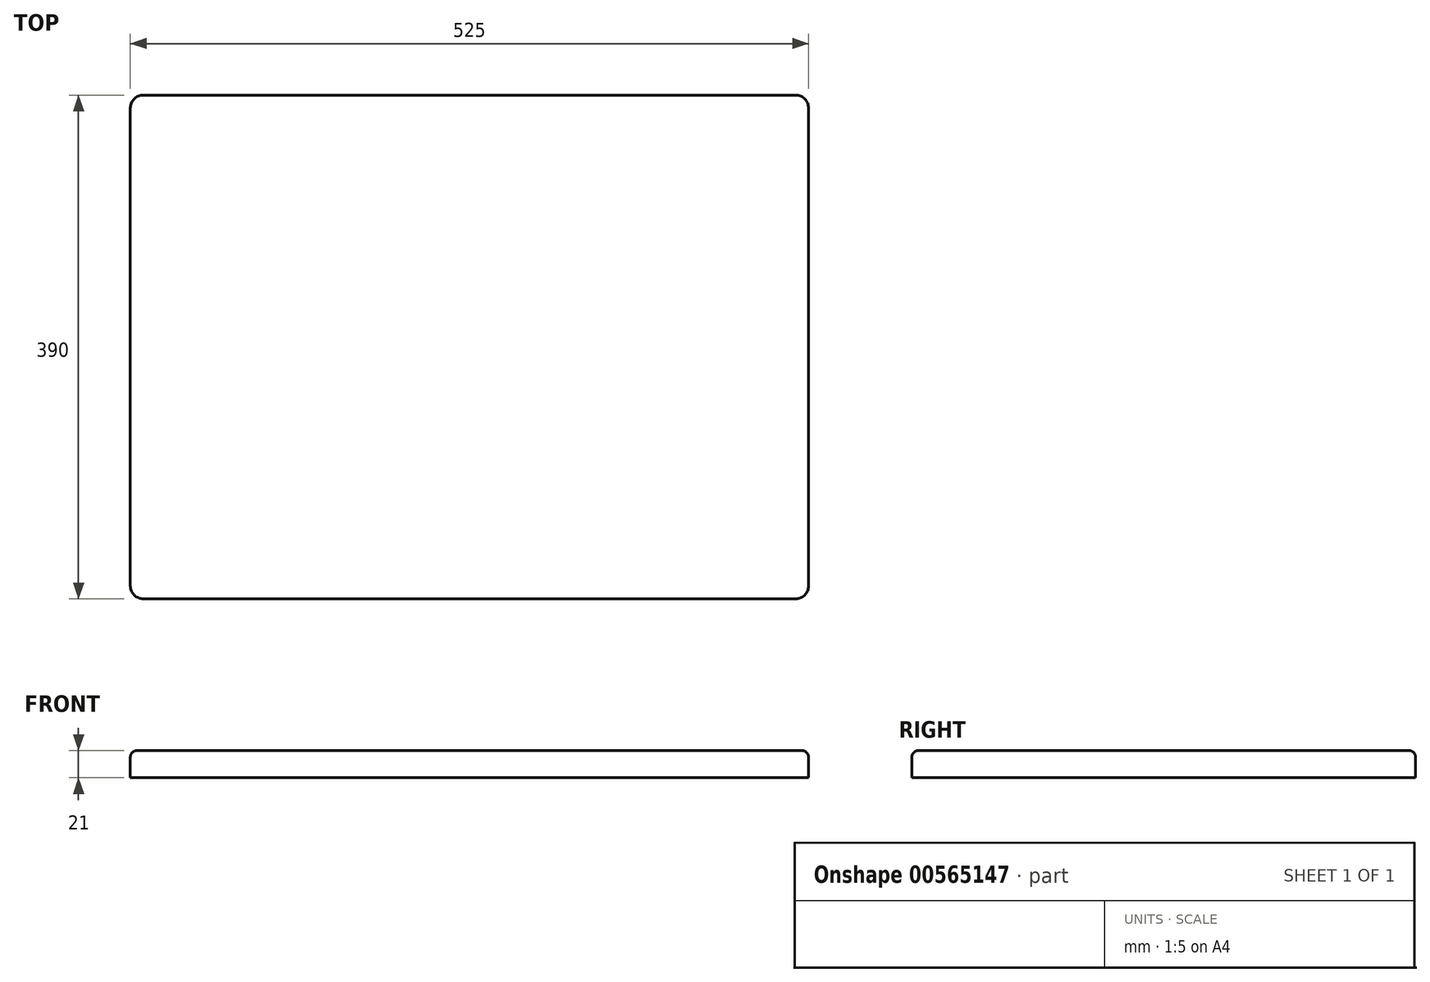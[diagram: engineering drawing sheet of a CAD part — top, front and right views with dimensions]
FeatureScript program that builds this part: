
annotation { "Feature Type Name" : "Feature", "Feature Type Description" : "" }
export const myFeature = defineFeature(function(context is Context, id is Id, definition is map)
    precondition{}
    {
        {
            var Q0;
            Q0=qCreatedBy(makeId("Top.planeOp"),FACE);
            var sketch = newSketch(context, id + "F0", { "sketchPlane" : qUnion([Q0])});
            skLineSegment(sketch, "E0.bottom", {"start": v(262.5, 195) * mm, "end": v(-262.5, 195) * mm});
            skLineSegment(sketch, "E0.top", {"start": v(262.5, -195) * mm, "end": v(-262.5, -195) * mm});
            skLineSegment(sketch, "E0.left", {"start": v(262.5, 195) * mm, "end": v(262.5, -195) * mm});
            skLineSegment(sketch, "E0.right", {"start": v(-262.5, 195) * mm, "end": v(-262.5, -195) * mm});
            skPoint(sketch, "E0.middle", {"position": v(0, 0) * mm});
            skSolve(sketch);
        }
        {
            var Q0;
            Q0=makeQuery(id+"F0.imprint","IMPRINT",FACE,{"disambiguationData":[TD([[makeQuery(id+"F0.imprint","IMPRINT",EDGE,{"derivedFrom":sQuery(id+"F0.wireOp",EDGE,"E0.bottom")}),1.0]])]});
            extrude(context, id + "F1", {"entities" : qUnion([Q0]), "depth" : 21 * mm, "offsetDistance" : 25 * mm});
        }
        {
            var Q0;
            Q0=makeQuery(id+"F1.opExtrude","SWEPT_EDGE",EDGE,{"disambiguationData":[OSD([sQuery(id+"F0.wireOp",EDGE,"E0.top"),sQuery(id+"F0.wireOp",EDGE,"E0.left")])]});
            var Q1;
            Q1=makeQuery(id+"F1.opExtrude","SWEPT_EDGE",EDGE,{"disambiguationData":[OSD([sQuery(id+"F0.wireOp",EDGE,"E0.bottom"),sQuery(id+"F0.wireOp",EDGE,"E0.left")])]});
            var Q2;
            Q2=makeQuery(id+"F1.opExtrude","SWEPT_EDGE",EDGE,{"disambiguationData":[OSD([sQuery(id+"F0.wireOp",EDGE,"E0.bottom"),sQuery(id+"F0.wireOp",EDGE,"E0.right")])]});
            var Q3;
            Q3=makeQuery(id+"F1.opExtrude","SWEPT_EDGE",EDGE,{"disambiguationData":[OSD([sQuery(id+"F0.wireOp",EDGE,"E0.top"),sQuery(id+"F0.wireOp",EDGE,"E0.right")])]});
            fillet(context, id + "F2", {"entities" : qUnion([Q0, Q1, Q2, Q3]), "radius" : 10 * mm, "tangentPropagation" : true, "allowEdgeOverflow" : false});
        }
        {
            var Q0;
            Q0=makeQuery(id+"F1.opExtrude","CAP_EDGE",EDGE,{"disambiguationData":[OSD([sQuery(id+"F0.wireOp",EDGE,"E0.left")])],"isStart":false});
            fillet(context, id + "F3", {"entities" : qUnion([Q0]), "radius" : 5 * mm, "tangentPropagation" : true, "allowEdgeOverflow" : false});
        }
    });
